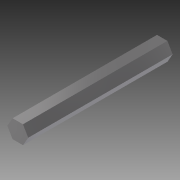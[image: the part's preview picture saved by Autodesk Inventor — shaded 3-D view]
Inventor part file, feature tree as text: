
AUTODESK INVENTOR PART (.ipt)
format: ipt  version: 2014 SP1 (Build 180222100, 222)  size: 75,776 bytes
history: native  units: in
note: dims shown in document units (in); Inventor stores cm internally (conversion verified against a paired STEP export)
features: extrude x1, sketch x1
ambient origin geometry x8: Origin, YZ Plane, XZ Plane, XY Plane, X Axis, Y Axis, Z Axis, Center Point
bodies: Solid1 (feature_tree)
feature tree (2):
  extrude  "Extrusion1"  Depth=3.0in TaperAngle=0.0deg
  sketch  "Sketch1"  dims[d0=0.375in d1=3.0in d2=0.0in]
